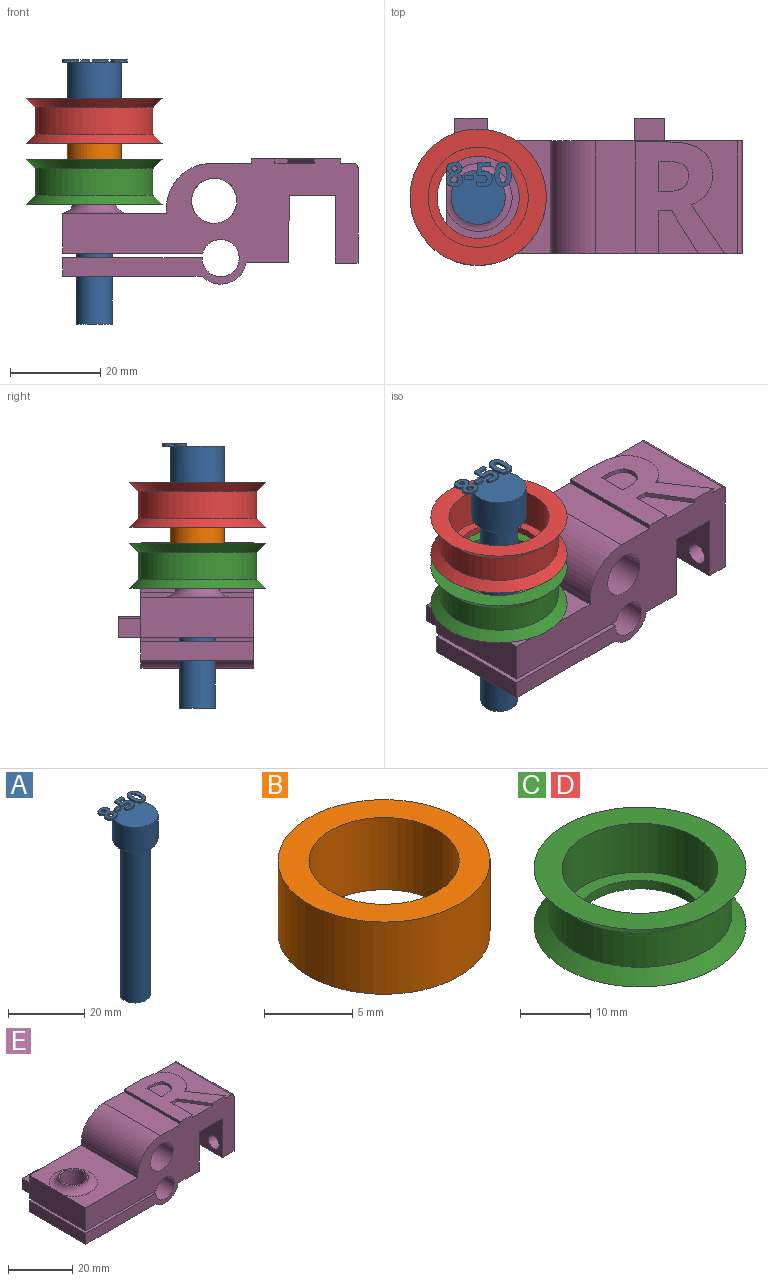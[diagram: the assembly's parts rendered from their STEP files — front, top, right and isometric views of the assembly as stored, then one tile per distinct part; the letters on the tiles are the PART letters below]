
ASSEMBLY  parts=5 mates=4
PART A: 86 faces, bbox 14.5x13.7x58.5 mm
  f0: plane 12x12mm, normal (0,0,1), area 99.4mm2, adj f5,f22,f23,f24,f25,f26,f40,f41
  f1: plane 1x0.26mm, normal (0,0,1), area 0.1mm2, adj f5,f46,f47,f48,f49
  f2: plane 0.85x0.68mm, normal (0,0,1), area 0.2mm2, adj f5,f29,f30,f31
  f3: cylinder r=4mm len=50mm, axis (0,0,-1), area 1256.6mm2, adj f4,f6
  f4: plane 8x8mm, normal (0,0,-1), area 50.3mm2, adj f3
  f5: cylinder r=6mm len=12mm, axis (0,0,-1), area 301.6mm2, adj f0,f1,f2,f6,f39,f45,f67,f85
  f6: plane 12x12mm, normal (0,0,-1), area 62.8mm2, adj f3,f5
  f7: extruded ~0.5x0.46mm, area 0.2mm2, adj f8,f37,f38,f39
  f8: extruded ~0.5x0.46mm, area 0.2mm2, adj f7,f9,f38,f39
  f9: extruded ~0.5x0.39mm, area 0.2mm2, adj f8,f10,f38,f39
  f10: extruded ~0.5x0.4mm, area 0.2mm2, adj f9,f11,f38,f39
  f11: extruded ~0.5x0.49mm, area 0.3mm2, adj f10,f12,f38,f39
  f12: extruded ~0.5x0.5mm, area 0.3mm2, adj f11,f13,f38,f39
  f13: extruded ~0.5x0.39mm, area 0.2mm2, adj f12,f37,f38,f39
  f14: extruded ~1.22x0.5mm, area 0.6mm2, adj f15,f35,f38,f39
  f15: extruded ~1.22x0.5mm, area 0.6mm2, adj f14,f16,f38,f39
  f16: extruded ~0.91x0.5mm, area 0.5mm2, adj f15,f17,f38,f39
  f17: extruded ~0.71x0.5mm, area 0.4mm2, adj f16,f18,f38,f39
  f18: extruded ~0.65x0.61mm, area 0.4mm2, adj f17,f19,f38,f39
  f19: extruded ~0.77x0.62mm, area 0.5mm2, adj f18,f20,f38,f39
  f20: extruded ~0.8x0.5mm, area 0.4mm2, adj f19,f21,f38,f39
  f21: extruded ~1.04x0.5mm, area 0.6mm2, adj f20,f22,f38,f39
  f22: extruded ~1.36x0.5mm, area 0.7mm2, adj f0,f21,f23,f38,f39
  f23: extruded ~1.33x0.5mm, area 0.7mm2, adj f0,f22,f24,f38
  f24: extruded ~1.04x0.51mm, area 0.6mm2, adj f0,f23,f25,f38
  f25: extruded ~0.75x0.5mm, area 0.4mm2, adj f0,f24,f26,f38
  f26: extruded ~0.85x0.66mm, area 0.5mm2, adj f0,f25,f27,f38,f39
  f27: extruded ~0.72x0.56mm, area 0.5mm2, adj f26,f28,f38,f39
  f28: extruded ~0.72x0.5mm, area 0.4mm2, adj f27,f35,f38,f39
  f29: extruded ~0.5x0.45mm, area 0.3mm2, adj f2,f30,f36,f38,f39
  f30: extruded ~0.5x0.47mm, area 0.3mm2, adj f2,f29,f31,f38
  f31: extruded ~0.62x0.5mm, area 0.3mm2, adj f2,f30,f32,f38,f39
  f32: extruded ~0.59x0.5mm, area 0.3mm2, adj f31,f33,f38,f39
  f33: extruded ~0.5x0.48mm, area 0.3mm2, adj f32,f34,f38,f39
  f34: extruded ~0.89x0.77mm, area 0.6mm2, adj f33,f36,f38,f39
  f35: extruded ~0.93x0.5mm, area 0.5mm2, adj f14,f28,f38,f39
  f36: extruded ~0.66x0.5mm, area 0.4mm2, adj f29,f34,f38,f39
  f37: extruded ~0.5x0.39mm, area 0.2mm2, adj f7,f13,f38,f39
  f38: plane 5.4x3.69mm, normal (0,0,1), area 12.7mm2, adj f7,f8,f9,f10,f11,f12,f13,f14
  f39: plane 5.4x3.53mm, normal (0,0,-1), area 10.2mm2, adj f5,f7,f8,f9,f10,f11,f12,f13
  f40: plane 0.9x0.5mm, normal (-1,0,0), area 0.4mm2, adj f0,f41,f43,f44
  f41: plane 1.93x0.5mm, normal (0,-1,0), area 1mm2, adj f0,f40,f42,f44
  f42: plane 0.9x0.5mm, normal (1,0,0), area 0.4mm2, adj f0,f41,f43,f44
  f43: plane 1.93x0.5mm, normal (0,1,0), area 1mm2, adj f0,f40,f42,f44
  f44: plane 1.93x0.9mm, normal (0,0,1), area 1.7mm2, adj f40,f41,f42,f43
  f45: plane 0.76x0.31mm, normal (0,0,-1), area 0mm2, adj f5,f46
  f46: extruded ~1.21x0.5mm, area 0.7mm2, adj f0,f1,f45,f47,f65,f66
  f47: extruded ~0.54x0.5mm, area 0.3mm2, adj f1,f46,f48,f66
  f48: plane 0.5x0.13mm, normal (-0.2,0.98,0), area 0.1mm2, adj f1,f47,f49,f66
  f49: plane 1.03x0.5mm, normal (1,-0.09,0), area 0.5mm2, adj f1,f48,f50,f66,f67
  f50: plane 1.88x0.5mm, normal (0,-1,0), area 0.9mm2, adj f49,f51,f66,f67
  f51: plane 0.94x0.5mm, normal (1,0,0), area 0.5mm2, adj f50,f52,f66,f67
  f52: plane 2.85x0.5mm, normal (0,1,0), area 1.4mm2, adj f51,f53,f66,f67
  f53: plane 2.68x0.5mm, normal (-1,0.07,0), area 1.3mm2, adj f0,f52,f54,f66,f67
  f54: plane 0.5x0.44mm, normal (-0.47,-0.88,0), area 0.3mm2, adj f0,f53,f55,f66
  f55: extruded ~0.5x0.37mm, area 0.2mm2, adj f0,f54,f56,f66
  f56: extruded ~0.5x0.42mm, area 0.2mm2, adj f0,f55,f57,f66
  f57: extruded ~1.05x0.8mm, area 0.8mm2, adj f0,f56,f58,f66
  f58: extruded ~1.02x0.83mm, area 0.8mm2, adj f0,f57,f59,f66
  f59: extruded ~0.72x0.5mm, area 0.4mm2, adj f0,f58,f60,f66
  f60: extruded ~0.66x0.5mm, area 0.4mm2, adj f0,f59,f61,f66
  f61: plane 0.96x0.5mm, normal (-1,0,0), area 0.5mm2, adj f0,f60,f62,f66
  f62: extruded ~1.42x0.5mm, area 0.7mm2, adj f0,f61,f63,f66
  f63: extruded ~1.55x0.5mm, area 0.8mm2, adj f0,f62,f64,f66
  f64: extruded ~1.36x0.54mm, area 0.8mm2, adj f0,f63,f65,f66
  f65: extruded ~1.17x0.5mm, area 0.6mm2, adj f0,f46,f64,f66
  f66: plane 5.33x3.51mm, normal (0,0,1), area 10.9mm2, adj f46,f47,f48,f49,f50,f51,f52,f53
  f67: plane 2.97x1.71mm, normal (0,0,-1), area 3.5mm2, adj f5,f49,f50,f51,f52,f53
  f68: extruded ~1.39x0.5mm, area 0.7mm2, adj f69,f83,f84,f85
  f69: extruded ~1.39x0.5mm, area 0.7mm2, adj f68,f70,f84,f85
  f70: extruded ~0.56x0.5mm, area 0.4mm2, adj f69,f71,f84,f85
  f71: extruded ~0.56x0.5mm, area 0.4mm2, adj f70,f72,f84,f85
  f72: extruded ~1.39x0.5mm, area 0.7mm2, adj f71,f73,f84,f85
  f73: extruded ~1.38x0.5mm, area 0.7mm2, adj f72,f74,f84,f85
  f74: extruded ~0.56x0.5mm, area 0.4mm2, adj f73,f83,f84,f85
  f75: extruded ~2.04x0.5mm, area 1.1mm2, adj f76,f82,f84,f85
  f76: extruded ~2.02x0.5mm, area 1.1mm2, adj f75,f77,f84,f85
  f77: extruded ~1.38x0.69mm, area 0.8mm2, adj f76,f78,f84,f85
  f78: extruded ~1.38x0.66mm, area 0.8mm2, adj f77,f79,f84,f85
  f79: extruded ~2.05x0.5mm, area 1.1mm2, adj f78,f80,f84,f85
  f80: extruded ~2.02x0.5mm, area 1mm2, adj f0,f79,f81,f84,f85
  f81: extruded ~1.37x0.68mm, area 0.8mm2, adj f0,f80,f82,f84
  f82: extruded ~1.39x0.66mm, area 0.8mm2, adj f0,f75,f81,f84,f85
  f83: extruded ~0.56x0.5mm, area 0.4mm2, adj f68,f74,f84,f85
  f84: plane 5.41x3.68mm, normal (0,0,1), area 12.1mm2, adj f68,f69,f70,f71,f72,f73,f74,f75
  f85: plane 5.41x3.68mm, normal (0,0,-1), area 10.3mm2, adj f5,f68,f69,f70,f71,f72,f73,f74
PART B: 4 faces, bbox 12x12x5 mm
  f0: cylinder r=4.25mm len=8.5mm, axis (0,0,-1), area 133.5mm2, adj f2,f3
  f1: cylinder r=6mm len=12mm, axis (0,0,-1), area 188.5mm2, adj f2,f3
  f2: plane 12x12mm, normal (0,0,1), area 56.4mm2, adj f0,f1
  f3: plane 12x12mm, normal (0,0,-1), area 56.4mm2, adj f0,f1
PART C: 8 faces, bbox 30.2x30.2x10 mm
  f0: plane 30.2x30.2mm, normal (0,0,1), area 329.2mm2, adj f1,f7
  f1: cylinder r=11.1mm len=22.2mm, axis (0,0,-1), area 592.8mm2, adj f0,f2
  f2: plane 22.2x22.2mm, normal (0,0,1), area 126.9mm2, adj f1,f3
  f3: cylinder r=9.1mm len=18.2mm, axis (0,0,-1), area 85.8mm2, adj f2,f4
  f4: plane 30.2x30.2mm, normal (0,0,-1), area 456.2mm2, adj f3,f5
  f5: cone r=13.1mm half-angle=45deg, axis (0,0,-1), area 250.6mm2, adj f4,f6
  f6: cylinder r=13.1mm len=26.2mm, axis (0,0,-1), area 493.9mm2, adj f5,f7
  f7: cone r=15.1mm half-angle=45deg, axis (0,0,1), area 250.6mm2, adj f0,f6
PART D: same geometry as C
PART E: 56 faces, bbox 68.9x30x27.7 mm
  f0: plane 31.42x25mm, normal (0,0,1), area 392.1mm2, adj f14,f15,f25,f27,f40,f41,f42,f43
  f1: plane 9.51x8.71mm, normal (0,0,1), area 54.7mm2, adj f14,f37,f38,f39
  f2: plane 25x4.12mm, normal (-1,0,0), area 103mm2, adj f5,f14,f15,f19
  f3: cylinder r=4.17mm len=8.35mm, axis (0,0,1), area 108.1mm2, adj f5,f19
  f4: plane 25x9.34mm, normal (0,0,-1), area 233.4mm2, adj f13,f14,f15,f17
  f5: plane 30.88x25mm, normal (0,0,-1), area 717.2mm2, adj f2,f3,f14,f15,f17
  f6: plane 25x8.82mm, normal (-1,0,0), area 219.6mm2, adj f7,f14,f15,f20,f24
  f7: plane 25x23mm, normal (0,0,1), area 400mm2, adj f6,f8,f14,f15,f24
  f8: plane 25x1.1mm, normal (-1,0,0), area 27.5mm2, adj f7,f14,f15,f25
  f9: plane 25x21.09mm, normal (1,0,0), area 493.5mm2, adj f10,f14,f15,f22,f23,f27
  f10: plane 25x5mm, normal (0,0,-1), area 125mm2, adj f9,f11,f14,f15
  f11: plane 25x15mm, normal (-1,0,0), area 341.3mm2, adj f10,f12,f14,f15,f22,f23
  f12: plane 25x10.2mm, normal (0,0,-1), area 255mm2, adj f11,f13,f14,f15
  f13: plane 25x14.91mm, normal (1,0,-0.01), area 372.8mm2, adj f4,f12,f14,f15
  f14: plane 65.42x27.75mm, normal (0,-1,0), area 988.1mm2, adj f0,f1,f2,f4,f5,f6,f7,f8
  f15: plane 65.42x26.75mm, normal (0,1,0), area 917.1mm2, adj f0,f2,f4,f5,f6,f7,f8,f9
  f16: cylinder r=4.17mm len=10.78mm, axis (0,0,1), area 282.8mm2, adj f20,f21
  f17: cylinder r=5.75mm len=25mm, axis (0,-1,0), area 315.9mm2, adj f4,f5,f14,f15
  f18: cylinder r=4.1mm len=25mm, axis (0,-1,0), area 618.7mm2, adj f14,f15,f19,f20
  f19: plane 30.91x25mm, normal (0,0,1), area 718.1mm2, adj f2,f3,f14,f15,f18
  f20: plane 31.07x30mm, normal (0,0,-1), area 758.4mm2, adj f6,f14,f15,f16,f18,f29,f30,f31
  f21: plane 9.35x9.35mm, normal (0,0,1), area 13.9mm2, adj f16,f24
  f22: cylinder r=2.43mm len=5mm, axis (1,0,0), area 76.2mm2, adj f9,f11
  f23: cylinder r=2.2mm len=5mm, axis (1,0,0), area 69.1mm2, adj f9,f11
  f24: torus R=7.5mm, axis (0,0,-1), area 134.6mm2, adj f6,f7,f21
  f25: cylinder r=10mm len=25mm, axis (0,-1,0), area 392.7mm2, adj f0,f8,f14,f15
  f26: cylinder r=5mm len=25mm, axis (0,-1,0), area 785.4mm2, adj f14,f15
  f27: cylinder r=1mm len=25mm, axis (0,-1,0), area 39.3mm2, adj f0,f9,f14,f15
  f28: plane 7.3x5mm, normal (0,0,1), area 36.5mm2, adj f15,f29,f30,f31
  f29: plane 5x4.12mm, normal (-1,0,0), area 20.6mm2, adj f15,f20,f28,f31
  f30: plane 5x4.12mm, normal (1,0,0), area 20.6mm2, adj f15,f20,f28,f31
  f31: plane 7.3x4.12mm, normal (0,1,0), area 30.1mm2, adj f20,f28,f29,f30
  f32: plane 6.63x5mm, normal (0,0,1), area 33.2mm2, adj f15,f33,f35,f36
  f33: plane 5x4.5mm, normal (-1,0,0), area 22.5mm2, adj f15,f32,f34,f36
  f34: plane 6.63x5mm, normal (0,0,-1), area 33.2mm2, adj f15,f33,f35,f36
  f35: plane 5x4.5mm, normal (1,0,0), area 22.5mm2, adj f15,f32,f34,f36
  f36: plane 6.63x4.5mm, normal (0,1,0), area 29.9mm2, adj f32,f33,f34,f35
  f37: plane 9.51x1mm, normal (1,0,0), area 9.5mm2, adj f1,f14,f38,f54
  f38: plane 2.79x1mm, normal (0,-1,0), area 2.8mm2, adj f1,f37,f39,f54
  f39: plane 9.51x5.92mm, normal (-0.85,-0.53,0), area 11.2mm2, adj f1,f14,f38,f54
  f40: extruded ~10.8x7.29mm, area 13mm2, adj f0,f14,f41,f54
  f41: extruded ~3.41x2.67mm, area 4.4mm2, adj f0,f40,f42,f54
  f42: extruded ~3.89x1.2mm, area 4.1mm2, adj f0,f41,f43,f54
  f43: extruded ~5.59x2.42mm, area 6.3mm2, adj f0,f42,f44,f54
  f44: extruded ~7.48x1.84mm, area 7.8mm2, adj f0,f43,f45,f54
  f45: plane 7.22x1mm, normal (0,1,0), area 7.2mm2, adj f0,f44,f46,f54
  f46: plane 24.79x1mm, normal (-1,0,0), area 24.8mm2, adj f0,f14,f45,f54
  f47: plane 1.69x1mm, normal (0,1,0), area 1.7mm2, adj f48,f53,f54,f55
  f48: plane 6.7x1mm, normal (1,0,0), area 6.7mm2, adj f47,f49,f54,f55
  f49: plane 1.6x1mm, normal (0,-1,0), area 1.6mm2, adj f48,f50,f54,f55
  f50: extruded ~3.75x1mm, area 3.9mm2, adj f49,f51,f54,f55
  f51: extruded ~2.51x1.21mm, area 2.9mm2, adj f50,f52,f54,f55
  f52: extruded ~2.61x1.19mm, area 3mm2, adj f51,f53,f54,f55
  f53: extruded ~3.68x1mm, area 3.8mm2, adj f47,f52,f54,f55
  f54: plane 24.79x19.8mm, normal (0,0,1), area 300mm2, adj f14,f37,f38,f39,f40,f41,f42,f43
  f55: plane 6.7x6.56mm, normal (0,0,1), area 38.8mm2, adj f47,f48,f49,f50,f51,f52,f53
PLACE A t=(-103.78,-12.5,-13.6)mm
PLACE B rot(axis=(1,0,0),180deg) t=(-103.78,-12.5,26.4)mm
PLACE C t=(-103.78,-12.5,18.1)mm
PLACE D t=(-103.78,-12.5,31.6)mm
PLACE E at identity
MATE fastened A.f3 <-> D.f1  axis (0,0,-1) through (-103.78,-12.5,36.4)mm
MATE fastened B.f0 <-> C.f1  axis (0,0,1) through (-103.78,-12.5,21.4)mm
MATE fastened C.f1 <-> E.f3  axis (0,0,-1) through (-103.78,-12.5,12.9)mm
MATE fastened D.f1 <-> B.f0  axis (0,0,-1) through (-103.78,-12.5,26.4)mm
